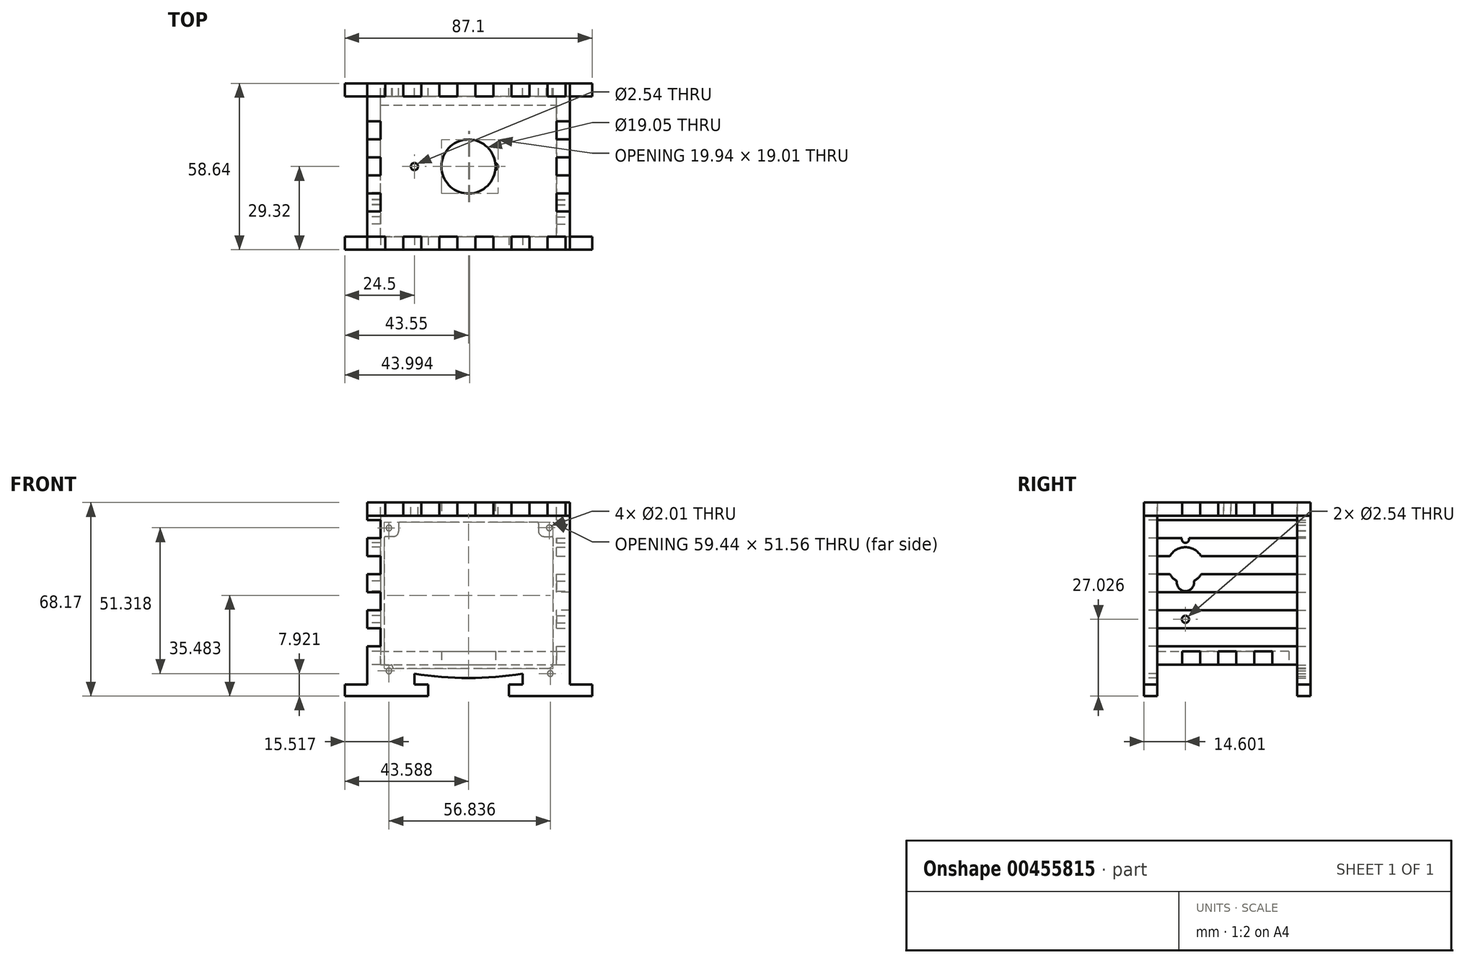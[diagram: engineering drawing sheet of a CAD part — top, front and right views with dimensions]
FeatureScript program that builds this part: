
annotation { "Feature Type Name" : "Feature", "Feature Type Description" : "" }
export const myFeature = defineFeature(function(context is Context, id is Id, definition is map)
    precondition{}
    {
        {
            var Q0;
            Q0=qCreatedBy(makeId("Top.planeOp"),FACE);
            var sketch = newSketch(context, id + "F0", { "sketchPlane" : qUnion([Q0])});
            skLineSegment(sketch, "E0.bottom", {"start": v(-35.67, 29.32) * mm, "end": v(35.67, 29.32) * mm});
            skLineSegment(sketch, "E0.top", {"start": v(-35.67, -29.32) * mm, "end": v(35.67, -29.32) * mm});
            skLineSegment(sketch, "E0.left", {"start": v(-35.67, 29.32) * mm, "end": v(-35.67, -29.32) * mm});
            skLineSegment(sketch, "E0.right", {"start": v(35.67, 29.32) * mm, "end": v(35.67, -29.32) * mm});
            skLineSegment(sketch, "E1", {"start": v(-35.67, 29.32) * mm, "end": v(35.67, -29.32) * mm, "construction": true});
            skSolve(sketch);
        }
        {
            var Q0;
            Q0 = qSketchRegion(id + "F0", true);
            extrude(context, id + "F1", {"entities" : qUnion([Q0]), "offsetDistance" : 25.4 * mm, "depth" : 4.67 * mm});
        }
        {
            var Q0;
            Q0=makeQuery(id+"F1.opExtrude","CAP_FACE",FACE,{"disambiguationData":[OSD([sQuery(id+"F0.wireOp",EDGE,"E0.bottom"),sQuery(id+"F0.wireOp",EDGE,"E0.top"),sQuery(id+"F0.wireOp",EDGE,"E0.left"),sQuery(id+"F0.wireOp",EDGE,"E0.right")])],"isStart":false});
            var sketch = newSketch(context, id + "F2", { "sketchPlane" : qUnion([Q0])});
            skCircle(sketch, "E2", {"center": v(0, 0) * mm, "radius": 2.8 * mm});
            skCircle(sketch, "E3", {"center": v(-19.05, 0) * mm, "radius": 1.27 * mm});
            skCircle(sketch, "E4", {"center": v(9.14, 0) * mm, "radius": 1.27 * mm});
            skSolve(sketch);
        }
        {
            var Q0;
            Q0 = qSketchRegion(id + "F2", true);
            extrude(context, id + "F3", {"entities" : qUnion([Q0]), "operationType" : NewBodyOperationType.REMOVE, "endBound" : BoundingType.THROUGH_ALL, "oppositeDirection" : true, "depth" : 25.4 * mm});
        }
        {
            var Q0;
            Q0=makeQuery(id+"F1.opExtrude","CAP_FACE",FACE,{"disambiguationData":[OSD([sQuery(id+"F0.wireOp",EDGE,"E0.bottom"),sQuery(id+"F0.wireOp",EDGE,"E0.top"),sQuery(id+"F0.wireOp",EDGE,"E0.left"),sQuery(id+"F0.wireOp",EDGE,"E0.right")])],"isStart":false});
            var sketch = newSketch(context, id + "F4", { "sketchPlane" : qUnion([Q0])});
            skArc(sketch, "E5", {"start": v(-5.6, -3) * mm, "mid": v(6.35, 0) * mm, "end": v(-5.6, 3) * mm});
            skArc(sketch, "E6", {"start": v(-5.6, 3) * mm, "mid": v(-9.14, 0) * mm, "end": v(-5.6, -3) * mm});
            skSolve(sketch);
        }
        {
            var Q0;
            Q0 = qSketchRegion(id + "F4", true);
            extrude(context, id + "F5", {"entities" : qUnion([Q0]), "operationType" : NewBodyOperationType.REMOVE, "endBound" : BoundingType.THROUGH_ALL, "oppositeDirection" : true, "depth" : 25.4 * mm});
        }
        {
            var Q0;
            Q0=makeQuery(id+"F1.opExtrude","CAP_FACE",FACE,{"disambiguationData":[OSD([sQuery(id+"F0.wireOp",EDGE,"E0.bottom"),sQuery(id+"F0.wireOp",EDGE,"E0.top"),sQuery(id+"F0.wireOp",EDGE,"E0.left"),sQuery(id+"F0.wireOp",EDGE,"E0.right")])],"isStart":false});
            var sketch = newSketch(context, id + "F6", { "sketchPlane" : qUnion([Q0])});
            skLineSegment(sketch, "E7.bottom", {"start": v(-35.67, 29.32) * mm, "end": v(-29.32, 29.32) * mm});
            skLineSegment(sketch, "E7.top", {"start": v(-35.67, 24.65) * mm, "end": v(-29.32, 24.65) * mm});
            skLineSegment(sketch, "E7.left", {"start": v(-35.67, 29.32) * mm, "end": v(-35.67, 24.65) * mm});
            skLineSegment(sketch, "E7.right", {"start": v(-29.32, 29.32) * mm, "end": v(-29.32, 24.65) * mm});
            skLineSegment(sketch, "E8.1.0.0", {"start": v(-22.97, 29.32) * mm, "end": v(-16.62, 29.32) * mm});
            skLineSegment(sketch, "E8.1.0.1", {"start": v(-22.97, 29.32) * mm, "end": v(-22.97, 24.65) * mm});
            skLineSegment(sketch, "E8.1.0.2", {"start": v(-16.62, 29.32) * mm, "end": v(-16.62, 24.65) * mm});
            skLineSegment(sketch, "E8.1.0.3", {"start": v(-22.97, 24.65) * mm, "end": v(-16.62, 24.65) * mm});
            skLineSegment(sketch, "E8.2.0.0", {"start": v(-10.27, 29.32) * mm, "end": v(-3.92, 29.32) * mm});
            skLineSegment(sketch, "E8.2.0.1", {"start": v(-10.27, 29.32) * mm, "end": v(-10.27, 24.65) * mm});
            skLineSegment(sketch, "E8.2.0.2", {"start": v(-3.92, 29.32) * mm, "end": v(-3.92, 24.65) * mm});
            skLineSegment(sketch, "E8.2.0.3", {"start": v(-10.27, 24.65) * mm, "end": v(-3.92, 24.65) * mm});
            skLineSegment(sketch, "E8.3.0.0", {"start": v(2.43, 29.32) * mm, "end": v(8.78, 29.32) * mm});
            skLineSegment(sketch, "E8.3.0.1", {"start": v(2.43, 29.32) * mm, "end": v(2.43, 24.65) * mm});
            skLineSegment(sketch, "E8.3.0.2", {"start": v(8.78, 29.32) * mm, "end": v(8.78, 24.65) * mm});
            skLineSegment(sketch, "E8.3.0.3", {"start": v(2.43, 24.65) * mm, "end": v(8.78, 24.65) * mm});
            skLineSegment(sketch, "E8.direction1", {"start": v(-35.67, 29.32) * mm, "end": v(-22.97, 29.32) * mm, "construction": true});
            skLineSegment(sketch, "E9.0.4.0", {"start": v(15.13, 29.32) * mm, "end": v(21.48, 29.32) * mm});
            skLineSegment(sketch, "E9.3.4.0", {"start": v(15.13, 29.32) * mm, "end": v(15.13, 24.65) * mm});
            skLineSegment(sketch, "E9.6.4.0", {"start": v(21.48, 29.32) * mm, "end": v(21.48, 24.65) * mm});
            skLineSegment(sketch, "E9.9.4.0", {"start": v(15.13, 24.65) * mm, "end": v(21.48, 24.65) * mm});
            skLineSegment(sketch, "E10.0.5.0", {"start": v(27.83, 29.32) * mm, "end": v(34.18, 29.32) * mm});
            skLineSegment(sketch, "E10.3.5.0", {"start": v(27.83, 29.32) * mm, "end": v(27.83, 24.65) * mm});
            skLineSegment(sketch, "E10.6.5.0", {"start": v(34.18, 29.32) * mm, "end": v(34.18, 24.65) * mm});
            skLineSegment(sketch, "E10.9.5.0", {"start": v(27.83, 24.65) * mm, "end": v(34.18, 24.65) * mm});
            skSolve(sketch);
        }
        {
            var Q0;
            Q0 = qSketchRegion(id + "F6", true);
            extrude(context, id + "F7", {"entities" : qUnion([Q0]), "operationType" : NewBodyOperationType.REMOVE, "oppositeDirection" : true, "depth" : 25.4 * mm});
        }
        {
            var Q0;
            Q0=makeQuery(id+"F1.opExtrude","CAP_FACE",FACE,{"disambiguationData":[OSD([sQuery(id+"F0.wireOp",EDGE,"E0.bottom"),sQuery(id+"F0.wireOp",EDGE,"E0.top"),sQuery(id+"F0.wireOp",EDGE,"E0.left"),sQuery(id+"F0.wireOp",EDGE,"E0.right")])],"isStart":false});
            var sketch = newSketch(context, id + "F8", { "sketchPlane" : qUnion([Q0])});
            skLineSegment(sketch, "E11.0.1.0", {"start": v(-35.67, -15.88) * mm, "end": v(-31, -15.88) * mm});
            skLineSegment(sketch, "E11.0.1.1", {"start": v(-31, -15.88) * mm, "end": v(-31, -9.53) * mm});
            skLineSegment(sketch, "E11.0.1.2", {"start": v(-35.67, -15.88) * mm, "end": v(-35.67, -9.53) * mm});
            skLineSegment(sketch, "E11.0.1.3", {"start": v(-35.67, -9.53) * mm, "end": v(-31, -9.53) * mm});
            skLineSegment(sketch, "E11.0.2.0", {"start": v(-35.67, -3.18) * mm, "end": v(-31, -3.18) * mm});
            skLineSegment(sketch, "E11.0.2.1", {"start": v(-31, -3.18) * mm, "end": v(-31, 3.17) * mm});
            skLineSegment(sketch, "E11.0.2.2", {"start": v(-35.67, -3.18) * mm, "end": v(-35.67, 3.17) * mm});
            skLineSegment(sketch, "E11.0.2.3", {"start": v(-35.67, 3.17) * mm, "end": v(-31, 3.17) * mm});
            skLineSegment(sketch, "E11.0.3.0", {"start": v(-35.67, 9.52) * mm, "end": v(-31, 9.52) * mm});
            skLineSegment(sketch, "E11.0.3.1", {"start": v(-31, 9.52) * mm, "end": v(-31, 15.87) * mm});
            skLineSegment(sketch, "E11.0.3.2", {"start": v(-35.67, 9.52) * mm, "end": v(-35.67, 15.87) * mm});
            skLineSegment(sketch, "E11.0.3.3", {"start": v(-35.67, 15.87) * mm, "end": v(-31, 15.87) * mm});
            skSolve(sketch);
        }
        {
            var Q0;
            Q0 = qSketchRegion(id + "F8", true);
            extrude(context, id + "F9", {"entities" : qUnion([Q0]), "operationType" : NewBodyOperationType.REMOVE, "endBound" : BoundingType.THROUGH_ALL, "oppositeDirection" : true, "depth" : 25.4 * mm});
        }
        {
            var Q0;
            Q0=makeQuery(id+"F9.boolean.opBoolean","COPY",FACE,{"derivedFrom":makeQuery(id+"F9.opExtrude","SWEPT_FACE",FACE,{"disambiguationData":[OSD([sQuery(id+"F8.wireOp",EDGE,"E11.0.3.1")])]})});
            var sketch = newSketch(context, id + "F10", { "sketchPlane" : qUnion([Q0])});
            skLineSegment(sketch, "E12.bottom", {"start": v(29.32, 4.67) * mm, "end": v(-29.32, 4.67) * mm});
            skLineSegment(sketch, "E12.top", {"start": v(29.32, -52.45) * mm, "end": v(-29.32, -52.45) * mm});
            skLineSegment(sketch, "E12.left", {"start": v(29.32, 4.67) * mm, "end": v(29.32, -52.45) * mm});
            skLineSegment(sketch, "E12.right", {"start": v(-29.32, 4.67) * mm, "end": v(-29.32, -52.45) * mm});
            skSolve(sketch);
        }
        {
            var Q0;
            Q0 = qSketchRegion(id + "F10", true);
            var Q1;
            {var subQ1=sQuery(id+"F0.wireOp",EDGE,"E0.left");Q1=makeQuery(id+"F9.boolean.opBoolean","SPLIT",FACE,{"disambiguationData":[TD([makeQuery(id+"F9.opExtrude","SWEPT_FACE",FACE,{"disambiguationData":[OSD([sQuery(id+"F8.wireOp",EDGE,"E11.0.2.3")])]})])],"derivedFrom":makeQuery(id+"F1.opExtrude","SWEPT_FACE",FACE,{"disambiguationData":[OSD([subQ1])]})});}
            extrude(context, id + "F11", {"entities" : qUnion([Q0]), "endBound" : BoundingType.UP_TO_SURFACE, "endBoundEntityFace" : qUnion([Q1]), "depth" : 25.4 * mm});
        }
        {
            var Q0;
            Q0=makeQuery(id+"F1.opExtrude","SWEPT_BODY",BODY,{"disambiguationData":[OSD([sQuery(id+"F0.wireOp",EDGE,"E0.bottom"),sQuery(id+"F0.wireOp",EDGE,"E0.top"),sQuery(id+"F0.wireOp",EDGE,"E0.left"),sQuery(id+"F0.wireOp",EDGE,"E0.right")])]});
            var Q1;
            Q1=makeQuery(id+"F11.opExtrude","SWEPT_BODY",BODY,{"disambiguationData":[OSD([sQuery(id+"F10.wireOp",EDGE,"E12.bottom"),sQuery(id+"F10.wireOp",EDGE,"E12.top"),sQuery(id+"F10.wireOp",EDGE,"E12.left"),sQuery(id+"F10.wireOp",EDGE,"E12.right")])]});
            booleanBodies(context, id + "F12", {"operationType" : BooleanOperationType.SUBTRACTION, "tools" : qUnion([Q0]), "targets" : qUnion([Q1]), "keepTools" : true});
        }
        {
            var Q0;
            Q0=makeQuery(id+"F11.opExtrude","CAP_FACE",FACE,{"disambiguationData":[OSD([sQuery(id+"F10.wireOp",EDGE,"E12.bottom"),sQuery(id+"F10.wireOp",EDGE,"E12.top"),sQuery(id+"F10.wireOp",EDGE,"E12.left"),sQuery(id+"F10.wireOp",EDGE,"E12.right")])],"isStart":false});
            var sketch = newSketch(context, id + "F13", { "sketchPlane" : qUnion([Q0])});
            skCircle(sketch, "E13", {"center": v(14.72, -8.28) * mm, "radius": 1.27 * mm});
            skCircle(sketch, "E14", {"center": v(14.72, -17.42) * mm, "radius": 2.8 * mm});
            skCircle(sketch, "E15", {"center": v(14.72, -36.47) * mm, "radius": 1.27 * mm});
            skSolve(sketch);
        }
        {
            var Q0;
            Q0 = qSketchRegion(id + "F13", true);
            extrude(context, id + "F14", {"entities" : qUnion([Q0]), "operationType" : NewBodyOperationType.REMOVE, "endBound" : BoundingType.THROUGH_ALL, "oppositeDirection" : true, "depth" : 25.4 * mm});
        }
        {
            var Q0;
            Q0=makeQuery(id+"F11.opExtrude","CAP_FACE",FACE,{"disambiguationData":[OSD([sQuery(id+"F10.wireOp",EDGE,"E12.bottom"),sQuery(id+"F10.wireOp",EDGE,"E12.top"),sQuery(id+"F10.wireOp",EDGE,"E12.left"),sQuery(id+"F10.wireOp",EDGE,"E12.right")])],"isStart":false});
            var sketch = newSketch(context, id + "F15", { "sketchPlane" : qUnion([Q0])});
            skArc(sketch, "E16", {"start": v(17.73, -23.02) * mm, "mid": v(14.72, -11.07) * mm, "end": v(11.71, -23.02) * mm});
            skArc(sketch, "E17", {"start": v(11.71, -23.02) * mm, "mid": v(14.72, -26.57) * mm, "end": v(17.73, -23.02) * mm});
            skSolve(sketch);
        }
        {
            var Q0;
            Q0 = qSketchRegion(id + "F15", true);
            extrude(context, id + "F16", {"entities" : qUnion([Q0]), "operationType" : NewBodyOperationType.REMOVE, "endBound" : BoundingType.THROUGH_ALL, "oppositeDirection" : true, "depth" : 25.4 * mm});
        }
        {
            var Q0;
            {var subQ3=sQuery(id+"F0.wireOp",EDGE,"E0.bottom");Q0=makeQuery(id+"F7.boolean.opBoolean","SPLIT",FACE,{"disambiguationData":[TD([makeQuery(id+"F7.opExtrude","SWEPT_FACE",FACE,{"disambiguationData":[OSD([sQuery(id+"F6.wireOp",EDGE,"E8.2.0.2")])]})])],"derivedFrom":makeQuery(id+"F1.opExtrude","SWEPT_FACE",FACE,{"disambiguationData":[OSD([subQ3])]})});}
            var sketch = newSketch(context, id + "F17", { "sketchPlane" : qUnion([Q0])});
            skLineSegment(sketch, "E18.bottom", {"start": v(35.67, 4.67) * mm, "end": v(-35.67, 4.67) * mm});
            skLineSegment(sketch, "E18.top", {"start": v(35.67, -63.5) * mm, "end": v(-35.67, -63.5) * mm});
            skLineSegment(sketch, "E18.left", {"start": v(35.67, 4.67) * mm, "end": v(35.67, -63.5) * mm});
            skLineSegment(sketch, "E18.right", {"start": v(-35.67, 4.67) * mm, "end": v(-35.67, -63.5) * mm});
            skSolve(sketch);
        }
        {
            var Q0;
            Q0 = qSketchRegion(id + "F17", true);
            var Q1;
            Q1=makeQuery(id+"F7.boolean.opBoolean","COPY",FACE,{"derivedFrom":makeQuery(id+"F7.opExtrude","SWEPT_FACE",FACE,{"disambiguationData":[OSD([sQuery(id+"F6.wireOp",EDGE,"E8.3.0.3")])]})});
            extrude(context, id + "F18", {"entities" : qUnion([Q0]), "endBound" : BoundingType.UP_TO_SURFACE, "oppositeDirection" : true, "endBoundEntityFace" : qUnion([Q1]), "depth" : 25.4 * mm, "offsetDistance" : 25.4 * mm});
        }
        {
            var Q0;
            Q0=makeQuery(id+"F18.opExtrude","CAP_FACE",FACE,{"disambiguationData":[OSD([sQuery(id+"F17.wireOp",EDGE,"E18.bottom"),sQuery(id+"F17.wireOp",EDGE,"E18.top"),sQuery(id+"F17.wireOp",EDGE,"E18.left"),sQuery(id+"F17.wireOp",EDGE,"E18.right")])],"isStart":true});
            var sketch = newSketch(context, id + "F19", { "sketchPlane" : qUnion([Q0])});
            skLineSegment(sketch, "E19", {"start": v(-14.22, -63.5) * mm, "end": v(-14.22, -59.48) * mm});
            skLineSegment(sketch, "E20", {"start": v(-14.22, -59.48) * mm, "end": v(-19.05, -59.48) * mm});
            skLineSegment(sketch, "E21", {"start": v(-19.05, -59.48) * mm, "end": v(-19.05, -55.63) * mm});
            skLineSegment(sketch, "E22", {"start": v(19.05, -55.63) * mm, "end": v(19.05, -59.44) * mm});
            skLineSegment(sketch, "E23", {"start": v(19.05, -59.44) * mm, "end": v(14.22, -59.44) * mm});
            skLineSegment(sketch, "E24", {"start": v(14.22, -59.44) * mm, "end": v(14.22, -63.5) * mm});
            skLineSegment(sketch, "E25", {"start": v(14.22, -63.5) * mm, "end": v(-14.22, -63.5) * mm});
            skArc(sketch, "E26", {"start": v(-19.05, -55.63) * mm, "mid": v(0, -57.17) * mm, "end": v(19.05, -55.63) * mm});
            skArc(sketch, "E27", {"start": v(-19.05, -55.63) * mm, "mid": v(0, -57.22) * mm, "end": v(19.05, -55.63) * mm});
            skSolve(sketch);
        }
        {
            var Q0;
            Q0 = qSketchRegion(id + "F19", true);
            extrude(context, id + "F20", {"entities" : qUnion([Q0]), "operationType" : NewBodyOperationType.REMOVE, "endBound" : BoundingType.THROUGH_ALL, "oppositeDirection" : true, "depth" : 25.4 * mm});
        }
        {
            var Q0;
            Q0=makeQuery(id+"F18.opExtrude","CAP_FACE",FACE,{"disambiguationData":[OSD([sQuery(id+"F17.wireOp",EDGE,"E18.bottom"),sQuery(id+"F17.wireOp",EDGE,"E18.top"),sQuery(id+"F17.wireOp",EDGE,"E18.left"),sQuery(id+"F17.wireOp",EDGE,"E18.right")])],"isStart":true});
            var sketch = newSketch(context, id + "F21", { "sketchPlane" : qUnion([Q0])});
            skLineSegment(sketch, "E28.bottom", {"start": v(35.67, -63.5) * mm, "end": v(43.55, -63.5) * mm});
            skLineSegment(sketch, "E28.top", {"start": v(35.67, -59.44) * mm, "end": v(43.55, -59.44) * mm});
            skLineSegment(sketch, "E28.left", {"start": v(35.67, -63.5) * mm, "end": v(35.67, -59.44) * mm});
            skLineSegment(sketch, "E28.right", {"start": v(43.55, -63.5) * mm, "end": v(43.55, -59.44) * mm});
            skLineSegment(sketch, "E29.bottom", {"start": v(-35.67, -63.5) * mm, "end": v(-43.55, -63.5) * mm});
            skLineSegment(sketch, "E29.top", {"start": v(-35.67, -59.44) * mm, "end": v(-43.55, -59.44) * mm});
            skLineSegment(sketch, "E29.left", {"start": v(-35.67, -63.5) * mm, "end": v(-35.67, -59.44) * mm});
            skLineSegment(sketch, "E29.right", {"start": v(-43.55, -63.5) * mm, "end": v(-43.55, -59.44) * mm});
            skSolve(sketch);
        }
        {
            var Q0;
            Q0 = qSketchRegion(id + "F21", true);
            var Q1;
            Q1=makeQuery(id+"F18.opExtrude","CAP_FACE",FACE,{"disambiguationData":[OSD([sQuery(id+"F17.wireOp",EDGE,"E18.bottom"),sQuery(id+"F17.wireOp",EDGE,"E18.top"),sQuery(id+"F17.wireOp",EDGE,"E18.left"),sQuery(id+"F17.wireOp",EDGE,"E18.right")])],"isStart":false});
            extrude(context, id + "F22", {"entities" : qUnion([Q0]), "operationType" : NewBodyOperationType.ADD, "endBound" : BoundingType.UP_TO_SURFACE, "oppositeDirection" : true, "endBoundEntityFace" : qUnion([Q1]), "depth" : 25.4 * mm, "offsetDistance" : 25.4 * mm});
        }
        {
            var Q0;
            Q0=makeQuery(id+"F1.opExtrude","SWEPT_BODY",BODY,{"disambiguationData":[OSD([sQuery(id+"F0.wireOp",EDGE,"E0.bottom"),sQuery(id+"F0.wireOp",EDGE,"E0.top"),sQuery(id+"F0.wireOp",EDGE,"E0.left"),sQuery(id+"F0.wireOp",EDGE,"E0.right")])]});
            var Q1;
            Q1=makeQuery(id+"F18.opExtrude","SWEPT_BODY",BODY,{"disambiguationData":[OSD([sQuery(id+"F17.wireOp",EDGE,"E18.bottom"),sQuery(id+"F17.wireOp",EDGE,"E18.top"),sQuery(id+"F17.wireOp",EDGE,"E18.left"),sQuery(id+"F17.wireOp",EDGE,"E18.right")])]});
            booleanBodies(context, id + "F23", {"operationType" : BooleanOperationType.SUBTRACTION, "tools" : qUnion([Q0]), "targets" : qUnion([Q1]), "keepTools" : true});
        }
        {
            var Q0;
            Q0=makeQuery(id+"F22.boolean.opBoolean","MERGE",FACE,{"derivedFrom":[makeQuery(id+"F18.opExtrude","CAP_FACE",FACE,{"disambiguationData":[OSD([sQuery(id+"F17.wireOp",EDGE,"E18.bottom"),sQuery(id+"F17.wireOp",EDGE,"E18.top"),sQuery(id+"F17.wireOp",EDGE,"E18.left"),sQuery(id+"F17.wireOp",EDGE,"E18.right")])],"isStart":true}),makeQuery(id+"F22.opExtrude","CAP_FACE",FACE,{"disambiguationData":[OSD([sQuery(id+"F21.wireOp",EDGE,"E28.bottom"),sQuery(id+"F21.wireOp",EDGE,"E28.top"),sQuery(id+"F21.wireOp",EDGE,"E28.left"),sQuery(id+"F21.wireOp",EDGE,"E28.right")])],"isStart":true}),makeQuery(id+"F22.opExtrude","CAP_FACE",FACE,{"disambiguationData":[OSD([sQuery(id+"F21.wireOp",EDGE,"E29.bottom"),sQuery(id+"F21.wireOp",EDGE,"E29.top"),sQuery(id+"F21.wireOp",EDGE,"E29.left"),sQuery(id+"F21.wireOp",EDGE,"E29.right")])],"isStart":true})]});
            var sketch = newSketch(context, id + "F24", { "sketchPlane" : qUnion([Q0])});
            skLineSegment(sketch, "E30", {"start": v(35.67, -27.38) * mm, "end": v(22.88, -27.38) * mm, "construction": true});
            skPoint(sketch, "E30.endSnap0", {"position": v(35.67, -27.38) * mm});
            skLineSegment(sketch, "E31.bottom", {"start": v(35.67, -26.92) * mm, "end": v(31, -26.92) * mm});
            skLineSegment(sketch, "E31.top", {"start": v(35.67, -33.27) * mm, "end": v(31, -33.27) * mm});
            skLineSegment(sketch, "E31.left", {"start": v(35.67, -26.92) * mm, "end": v(35.67, -33.27) * mm});
            skLineSegment(sketch, "E31.right", {"start": v(31, -26.92) * mm, "end": v(31, -33.27) * mm});
            skLineSegment(sketch, "E32.bottom", {"start": v(31, -20.57) * mm, "end": v(35.67, -20.57) * mm});
            skLineSegment(sketch, "E32.top", {"start": v(31, -14.22) * mm, "end": v(35.67, -14.22) * mm});
            skLineSegment(sketch, "E32.left", {"start": v(31, -20.57) * mm, "end": v(31, -14.22) * mm});
            skLineSegment(sketch, "E32.right", {"start": v(35.67, -20.57) * mm, "end": v(35.67, -14.22) * mm});
            skLineSegment(sketch, "E33.0.1.0", {"start": v(31, -1.52) * mm, "end": v(35.67, -1.52) * mm});
            skLineSegment(sketch, "E33.0.1.1", {"start": v(31, -7.87) * mm, "end": v(31, -1.52) * mm});
            skLineSegment(sketch, "E33.0.1.2", {"start": v(35.67, -7.87) * mm, "end": v(35.67, -1.52) * mm});
            skLineSegment(sketch, "E33.0.1.3", {"start": v(31, -7.87) * mm, "end": v(35.67, -7.87) * mm});
            skLineSegment(sketch, "E33.direction1", {"start": v(31, -14.22) * mm, "end": v(53.97, -14.22) * mm, "construction": true});
            skLineSegment(sketch, "E33.direction2", {"start": v(31, -14.22) * mm, "end": v(31, -1.52) * mm, "construction": true});
            skLineSegment(sketch, "E34.MirrorCS", {"start": v(31, -40.54) * mm, "end": v(31, -53.24) * mm, "construction": true});
            skLineSegment(sketch, "E35.bottom", {"start": v(31, -39.62) * mm, "end": v(35.67, -39.62) * mm});
            skLineSegment(sketch, "E35.top", {"start": v(31, -45.97) * mm, "end": v(35.67, -45.97) * mm});
            skLineSegment(sketch, "E35.left", {"start": v(31, -39.62) * mm, "end": v(31, -45.97) * mm});
            skLineSegment(sketch, "E35.right", {"start": v(35.67, -39.62) * mm, "end": v(35.67, -45.97) * mm});
            skSolve(sketch);
        }
        {
            var Q0;
            Q0 = qSketchRegion(id + "F24", true);
            extrude(context, id + "F25", {"entities" : qUnion([Q0]), "operationType" : NewBodyOperationType.REMOVE, "endBound" : BoundingType.THROUGH_ALL, "oppositeDirection" : true, "depth" : 25.4 * mm});
        }
        {
            var Q0;
            Q0=makeQuery(id+"F18.opExtrude","SWEPT_BODY",BODY,{"disambiguationData":[OSD([sQuery(id+"F17.wireOp",EDGE,"E18.bottom"),sQuery(id+"F17.wireOp",EDGE,"E18.top"),sQuery(id+"F17.wireOp",EDGE,"E18.left"),sQuery(id+"F17.wireOp",EDGE,"E18.right")])]});
            var Q1;
            Q1=makeQuery(id+"F11.opExtrude","SWEPT_BODY",BODY,{"disambiguationData":[OSD([sQuery(id+"F10.wireOp",EDGE,"E12.bottom"),sQuery(id+"F10.wireOp",EDGE,"E12.top"),sQuery(id+"F10.wireOp",EDGE,"E12.left"),sQuery(id+"F10.wireOp",EDGE,"E12.right")])]});
            booleanBodies(context, id + "F26", {"operationType" : BooleanOperationType.SUBTRACTION, "tools" : qUnion([Q0]), "targets" : qUnion([Q1]), "keepTools" : true});
        }
        {
            var Q0;
            Q0=makeQuery(id+"F11.opExtrude","CAP_FACE",FACE,{"disambiguationData":[OSD([sQuery(id+"F10.wireOp",EDGE,"E12.bottom"),sQuery(id+"F10.wireOp",EDGE,"E12.top"),sQuery(id+"F10.wireOp",EDGE,"E12.left"),sQuery(id+"F10.wireOp",EDGE,"E12.right")])],"isStart":false});
            var sketch = newSketch(context, id + "F27", { "sketchPlane" : qUnion([Q0])});
            skLineSegment(sketch, "E36.bottom", {"start": v(-15.87, -47.78) * mm, "end": v(-9.52, -47.78) * mm});
            skLineSegment(sketch, "E36.top", {"start": v(-15.87, -52.45) * mm, "end": v(-9.52, -52.45) * mm});
            skLineSegment(sketch, "E36.left", {"start": v(-15.87, -47.78) * mm, "end": v(-15.87, -52.45) * mm});
            skLineSegment(sketch, "E36.right", {"start": v(-9.52, -47.78) * mm, "end": v(-9.52, -52.45) * mm});
            skLineSegment(sketch, "E37.bottom", {"start": v(-3.17, -47.78) * mm, "end": v(3.18, -47.78) * mm});
            skLineSegment(sketch, "E37.top", {"start": v(-3.17, -52.45) * mm, "end": v(3.18, -52.45) * mm});
            skLineSegment(sketch, "E37.left", {"start": v(-3.17, -47.78) * mm, "end": v(-3.17, -52.45) * mm});
            skLineSegment(sketch, "E37.right", {"start": v(3.18, -47.78) * mm, "end": v(3.18, -52.45) * mm});
            skLineSegment(sketch, "E38.bottom", {"start": v(9.53, -47.78) * mm, "end": v(15.88, -47.78) * mm});
            skLineSegment(sketch, "E38.top", {"start": v(9.53, -52.45) * mm, "end": v(15.88, -52.45) * mm});
            skLineSegment(sketch, "E38.left", {"start": v(9.53, -47.78) * mm, "end": v(9.53, -52.45) * mm});
            skLineSegment(sketch, "E38.right", {"start": v(15.88, -47.78) * mm, "end": v(15.88, -52.45) * mm});
            skSolve(sketch);
        }
        {
            var Q0;
            Q0 = qSketchRegion(id + "F27", true);
            var Q1;
            Q1=makeQuery(id+"F11.opExtrude","CAP_FACE",FACE,{"disambiguationData":[OSD([sQuery(id+"F10.wireOp",EDGE,"E12.bottom"),sQuery(id+"F10.wireOp",EDGE,"E12.top"),sQuery(id+"F10.wireOp",EDGE,"E12.left"),sQuery(id+"F10.wireOp",EDGE,"E12.right")])],"isStart":true});
            extrude(context, id + "F28", {"entities" : qUnion([Q0]), "operationType" : NewBodyOperationType.REMOVE, "endBound" : BoundingType.UP_TO_SURFACE, "oppositeDirection" : true, "depth" : 25.4 * mm, "endBoundEntityFace" : qUnion([Q1]), "offsetDistance" : 25.4 * mm});
        }
        {
            var Q0;
            Q0=makeQuery(id+"F11.opExtrude","SWEPT_BODY",BODY,{"disambiguationData":[OSD([sQuery(id+"F10.wireOp",EDGE,"E12.bottom"),sQuery(id+"F10.wireOp",EDGE,"E12.top"),sQuery(id+"F10.wireOp",EDGE,"E12.left"),sQuery(id+"F10.wireOp",EDGE,"E12.right")])]});
            var Q1;
            Q1=qCreatedBy(makeId("Right.planeOp"),FACE);
            mirror(context, id + "F29", {"entities" : qUnion([Q0]), "mirrorPlane" : qUnion([Q1])});
        }
        {
            var Q0;
            Q0=makeQuery(id+"F29.opPattern","COPY",BODY,{"derivedFrom":makeQuery(id+"F11.opExtrude","SWEPT_BODY",BODY,{"disambiguationData":[OSD([sQuery(id+"F10.wireOp",EDGE,"E12.bottom"),sQuery(id+"F10.wireOp",EDGE,"E12.top"),sQuery(id+"F10.wireOp",EDGE,"E12.left"),sQuery(id+"F10.wireOp",EDGE,"E12.right")])]}),"instanceName":"1"});
            var Q1;
            Q1=makeQuery(id+"F18.opExtrude","SWEPT_BODY",BODY,{"disambiguationData":[OSD([sQuery(id+"F17.wireOp",EDGE,"E18.bottom"),sQuery(id+"F17.wireOp",EDGE,"E18.top"),sQuery(id+"F17.wireOp",EDGE,"E18.left"),sQuery(id+"F17.wireOp",EDGE,"E18.right")])]});
            booleanBodies(context, id + "F30", {"operationType" : BooleanOperationType.SUBTRACTION, "tools" : qUnion([Q0]), "targets" : qUnion([Q1]), "keepTools" : true});
        }
        {
            var Q0;
            Q0=makeQuery(id+"F18.opExtrude","SWEPT_BODY",BODY,{"disambiguationData":[OSD([sQuery(id+"F17.wireOp",EDGE,"E18.bottom"),sQuery(id+"F17.wireOp",EDGE,"E18.top"),sQuery(id+"F17.wireOp",EDGE,"E18.left"),sQuery(id+"F17.wireOp",EDGE,"E18.right")])]});
            var Q1;
            Q1=qCreatedBy(makeId("Front.planeOp"),FACE);
            mirror(context, id + "F31", {"entities" : qUnion([Q0]), "mirrorPlane" : qUnion([Q1])});
        }
        {
            var Q0;
            Q0=makeQuery(id+"F22.boolean.opBoolean","MERGE",FACE,{"derivedFrom":[makeQuery(id+"F18.opExtrude","CAP_FACE",FACE,{"disambiguationData":[OSD([sQuery(id+"F17.wireOp",EDGE,"E18.bottom"),sQuery(id+"F17.wireOp",EDGE,"E18.top"),sQuery(id+"F17.wireOp",EDGE,"E18.left"),sQuery(id+"F17.wireOp",EDGE,"E18.right")])],"isStart":true}),makeQuery(id+"F22.opExtrude","CAP_FACE",FACE,{"disambiguationData":[OSD([sQuery(id+"F21.wireOp",EDGE,"E28.bottom"),sQuery(id+"F21.wireOp",EDGE,"E28.top"),sQuery(id+"F21.wireOp",EDGE,"E28.left"),sQuery(id+"F21.wireOp",EDGE,"E28.right")])],"isStart":true}),makeQuery(id+"F22.opExtrude","CAP_FACE",FACE,{"disambiguationData":[OSD([sQuery(id+"F21.wireOp",EDGE,"E29.bottom"),sQuery(id+"F21.wireOp",EDGE,"E29.top"),sQuery(id+"F21.wireOp",EDGE,"E29.left"),sQuery(id+"F21.wireOp",EDGE,"E29.right")])],"isStart":true})]});
            var sketch = newSketch(context, id + "F32", { "sketchPlane" : qUnion([Q0])});
            skLineSegment(sketch, "E39", {"start": v(0, 8) * mm, "end": v(0, -66.28) * mm, "construction": true});
            skCircle(sketch, "E40", {"center": v(-27.74, -4.01) * mm, "radius": 1 * mm});
            skPoint(sketch, "E40.centerSnap0", {"position": v(-33.34, -5.9) * mm});
            skCircle(sketch, "E41", {"center": v(27.74, -4.01) * mm, "radius": 1 * mm});
            skCircle(sketch, "E42", {"center": v(28.75, -55.37) * mm, "radius": 1 * mm});
            skCircle(sketch, "E43", {"center": v(-29.2, -55.9) * mm, "radius": 1 * mm});
            skSolve(sketch);
        }
        {
            var Q0;
            Q0=makeQuery(id+"F22.boolean.opBoolean","MERGE",FACE,{"derivedFrom":[makeQuery(id+"F18.opExtrude","CAP_FACE",FACE,{"disambiguationData":[OSD([sQuery(id+"F17.wireOp",EDGE,"E18.bottom"),sQuery(id+"F17.wireOp",EDGE,"E18.top"),sQuery(id+"F17.wireOp",EDGE,"E18.left"),sQuery(id+"F17.wireOp",EDGE,"E18.right")])],"isStart":true}),makeQuery(id+"F22.opExtrude","CAP_FACE",FACE,{"disambiguationData":[OSD([sQuery(id+"F21.wireOp",EDGE,"E28.bottom"),sQuery(id+"F21.wireOp",EDGE,"E28.top"),sQuery(id+"F21.wireOp",EDGE,"E28.left"),sQuery(id+"F21.wireOp",EDGE,"E28.right")])],"isStart":true}),makeQuery(id+"F22.opExtrude","CAP_FACE",FACE,{"disambiguationData":[OSD([sQuery(id+"F21.wireOp",EDGE,"E29.bottom"),sQuery(id+"F21.wireOp",EDGE,"E29.top"),sQuery(id+"F21.wireOp",EDGE,"E29.left"),sQuery(id+"F21.wireOp",EDGE,"E29.right")])],"isStart":true})]});
            var sketch = newSketch(context, id + "F33", { "sketchPlane" : qUnion([Q0])});
            skLineSegment(sketch, "E44.bottom", {"start": v(-24.17, -2.24) * mm, "end": v(24.1, -2.24) * mm});
            skLineSegment(sketch, "E44.top", {"start": v(-27.85, -53.8) * mm, "end": v(26.24, -53.8) * mm});
            skLineSegment(sketch, "E44.left", {"start": v(-29.76, -7.82) * mm, "end": v(-29.76, -51.9) * mm});
            skLineSegment(sketch, "E44.right", {"start": v(29.68, -7.82) * mm, "end": v(29.68, -52.02) * mm});
            skPoint(sketch, "E45", {"position": v(-27.72, -4.27) * mm});
            skLineSegment(sketch, "E46", {"start": v(-24.68, -2.74) * mm, "end": v(-24.68, -5.41) * mm});
            skLineSegment(sketch, "E47", {"start": v(-26.58, -7.32) * mm, "end": v(-29.25, -7.32) * mm});
            skLineSegment(sketch, "E48", {"start": v(24.6, -2.74) * mm, "end": v(24.6, -5.41) * mm});
            skLineSegment(sketch, "E49", {"start": v(26.5, -7.32) * mm, "end": v(29.17, -7.32) * mm});
            skPoint(sketch, "E50.visualSharp", {"position": v(-24.68, -7.32) * mm});
            skArc(sketch, "E50.filletArc", {"start": v(-26.58, -7.32) * mm, "mid": v(-25.23, -6.76) * mm, "end": v(-24.68, -5.41) * mm});
            skPoint(sketch, "E51.visualSharp", {"position": v(24.6, -7.32) * mm});
            skArc(sketch, "E51.filletArc", {"start": v(24.6, -5.41) * mm, "mid": v(25.16, -6.76) * mm, "end": v(26.5, -7.32) * mm});
            skPoint(sketch, "E52.visualSharp", {"position": v(-29.76, -53.8) * mm});
            skArc(sketch, "E52.filletArc", {"start": v(-29.76, -51.9) * mm, "mid": v(-29.2, -53.24) * mm, "end": v(-27.85, -53.8) * mm});
            skPoint(sketch, "E53.visualSharp", {"position": v(29.68, -53.8) * mm});
            skCircle(sketch, "E54", {"center": v(28.03, -4.32) * mm, "radius": 1 * mm});
            skCircle(sketch, "E55", {"center": v(-28.45, -4.26) * mm, "radius": 1 * mm});
            skCircle(sketch, "E56", {"center": v(-28.8, -55.58) * mm, "radius": 1 * mm});
            skCircle(sketch, "E57", {"center": v(28.02, -54.66) * mm, "radius": 1 * mm});
            skLineSegment(sketch, "E58", {"start": v(29.17, -52.53) * mm, "end": v(27.26, -52.53) * mm});
            skLineSegment(sketch, "E59", {"start": v(26.75, -53.04) * mm, "end": v(26.75, -53.29) * mm});
            skArc(sketch, "E60.filletArc", {"start": v(29.17, -52.53) * mm, "mid": v(29.53, -52.38) * mm, "end": v(29.68, -52.02) * mm});
            skPoint(sketch, "E61.visualSharp", {"position": v(26.75, -52.53) * mm});
            skArc(sketch, "E61.filletArc", {"start": v(27.26, -52.53) * mm, "mid": v(26.9, -52.68) * mm, "end": v(26.75, -53.04) * mm});
            skArc(sketch, "E62.filletArc", {"start": v(26.24, -53.8) * mm, "mid": v(26.6, -53.65) * mm, "end": v(26.75, -53.29) * mm});
            skPoint(sketch, "E63.visualSharp", {"position": v(-24.68, -2.24) * mm});
            skArc(sketch, "E63.filletArc", {"start": v(-24.17, -2.24) * mm, "mid": v(-24.53, -2.38) * mm, "end": v(-24.68, -2.74) * mm});
            skPoint(sketch, "E64.visualSharp", {"position": v(-29.76, -7.32) * mm});
            skArc(sketch, "E64.filletArc", {"start": v(-29.25, -7.32) * mm, "mid": v(-29.6, -7.46) * mm, "end": v(-29.76, -7.82) * mm});
            skPoint(sketch, "E65.visualSharp", {"position": v(24.6, -2.24) * mm});
            skArc(sketch, "E65.filletArc", {"start": v(24.6, -2.74) * mm, "mid": v(24.45, -2.38) * mm, "end": v(24.1, -2.24) * mm});
            skPoint(sketch, "E66.visualSharp", {"position": v(29.68, -7.32) * mm});
            skArc(sketch, "E66.filletArc", {"start": v(29.68, -7.82) * mm, "mid": v(29.53, -7.46) * mm, "end": v(29.17, -7.32) * mm});
            skSolve(sketch);
        }
        {
            var Q0;
            Q0 = qSketchRegion(id + "F33", true);
            var Q1;
            Q1=makeQuery(id+"F22.boolean.opBoolean","MERGE",FACE,{"derivedFrom":[makeQuery(id+"F18.opExtrude","CAP_FACE",FACE,{"disambiguationData":[OSD([sQuery(id+"F17.wireOp",EDGE,"E18.bottom"),sQuery(id+"F17.wireOp",EDGE,"E18.top"),sQuery(id+"F17.wireOp",EDGE,"E18.left"),sQuery(id+"F17.wireOp",EDGE,"E18.right")])],"isStart":false}),makeQuery(id+"F22.opExtrude","CAP_FACE",FACE,{"disambiguationData":[OSD([sQuery(id+"F21.wireOp",EDGE,"E28.bottom"),sQuery(id+"F21.wireOp",EDGE,"E28.top"),sQuery(id+"F21.wireOp",EDGE,"E28.left"),sQuery(id+"F21.wireOp",EDGE,"E28.right")])],"isStart":false}),makeQuery(id+"F22.opExtrude","CAP_FACE",FACE,{"disambiguationData":[OSD([sQuery(id+"F21.wireOp",EDGE,"E29.bottom"),sQuery(id+"F21.wireOp",EDGE,"E29.top"),sQuery(id+"F21.wireOp",EDGE,"E29.left"),sQuery(id+"F21.wireOp",EDGE,"E29.right")])],"isStart":false})]});
            extrude(context, id + "F34", {"entities" : qUnion([Q0]), "operationType" : NewBodyOperationType.REMOVE, "endBound" : BoundingType.UP_TO_SURFACE, "oppositeDirection" : true, "endBoundEntityFace" : qUnion([Q1]), "depth" : 25.4 * mm, "offsetDistance" : 25.4 * mm});
        }
        {
            var Q0;
            Q0=makeQuery(id+"F31.opPattern","COPY",BODY,{"derivedFrom":makeQuery(id+"F18.opExtrude","SWEPT_BODY",BODY,{"disambiguationData":[OSD([sQuery(id+"F17.wireOp",EDGE,"E18.bottom"),sQuery(id+"F17.wireOp",EDGE,"E18.top"),sQuery(id+"F17.wireOp",EDGE,"E18.left"),sQuery(id+"F17.wireOp",EDGE,"E18.right")])]}),"instanceName":"1"});
            var Q1;
            Q1=makeQuery(id+"F11.opExtrude","SWEPT_BODY",BODY,{"disambiguationData":[OSD([sQuery(id+"F10.wireOp",EDGE,"E12.bottom"),sQuery(id+"F10.wireOp",EDGE,"E12.top"),sQuery(id+"F10.wireOp",EDGE,"E12.left"),sQuery(id+"F10.wireOp",EDGE,"E12.right")])]});
            var Q2;
            Q2=makeQuery(id+"F29.opPattern","COPY",BODY,{"derivedFrom":makeQuery(id+"F11.opExtrude","SWEPT_BODY",BODY,{"disambiguationData":[OSD([sQuery(id+"F10.wireOp",EDGE,"E12.bottom"),sQuery(id+"F10.wireOp",EDGE,"E12.top"),sQuery(id+"F10.wireOp",EDGE,"E12.left"),sQuery(id+"F10.wireOp",EDGE,"E12.right")])]}),"instanceName":"1"});
            booleanBodies(context, id + "F35", {"operationType" : BooleanOperationType.SUBTRACTION, "tools" : qUnion([Q0]), "targets" : qUnion([Q1, Q2]), "keepTools" : true});
        }
        {
            var Q0;
            Q0=makeQuery(id+"F31.opPattern","COPY",FACE,{"derivedFrom":makeQuery(id+"F22.boolean.opBoolean","MERGE",FACE,{"derivedFrom":[makeQuery(id+"F18.opExtrude","CAP_FACE",FACE,{"disambiguationData":[OSD([sQuery(id+"F17.wireOp",EDGE,"E18.bottom"),sQuery(id+"F17.wireOp",EDGE,"E18.top"),sQuery(id+"F17.wireOp",EDGE,"E18.left"),sQuery(id+"F17.wireOp",EDGE,"E18.right")])],"isStart":true}),makeQuery(id+"F22.opExtrude","CAP_FACE",FACE,{"disambiguationData":[OSD([sQuery(id+"F21.wireOp",EDGE,"E28.bottom"),sQuery(id+"F21.wireOp",EDGE,"E28.top"),sQuery(id+"F21.wireOp",EDGE,"E28.left"),sQuery(id+"F21.wireOp",EDGE,"E28.right")])],"isStart":true}),makeQuery(id+"F22.opExtrude","CAP_FACE",FACE,{"disambiguationData":[OSD([sQuery(id+"F21.wireOp",EDGE,"E29.bottom"),sQuery(id+"F21.wireOp",EDGE,"E29.top"),sQuery(id+"F21.wireOp",EDGE,"E29.left"),sQuery(id+"F21.wireOp",EDGE,"E29.right")])],"isStart":true})]}),"instanceName":"1"});
            var sketch = newSketch(context, id + "F36", { "sketchPlane" : qUnion([Q0])});
            skText(sketch, "E67", { "text": "B", "fontName": "OpenSans-Regular.ttf"});
            const initialGuessF36  = {"E67": [-0.0105, -0.03906, 1, 0, 0.02639]};
            skSetInitialGuess(sketch, initialGuessF36);
            skSolve(sketch);
        }
        {
            var Q0;
            Q0=makeQuery(id+"F11.opExtrude","SWEPT_FACE",FACE,{"disambiguationData":[OSD([sQuery(id+"F10.wireOp",EDGE,"E12.top")])]});
            var sketch = newSketch(context, id + "F37", { "sketchPlane" : qUnion([Q0])});
            skLineSegment(sketch, "E68.bottom", {"start": v(-35.67, 24.65) * mm, "end": v(35.67, 24.65) * mm});
            skLineSegment(sketch, "E68.top", {"start": v(-35.67, -21.65) * mm, "end": v(35.67, -21.65) * mm});
            skLineSegment(sketch, "E68.left", {"start": v(-35.67, 24.65) * mm, "end": v(-35.67, -21.65) * mm});
            skLineSegment(sketch, "E68.right", {"start": v(35.67, 24.65) * mm, "end": v(35.67, -21.65) * mm});
            skSolve(sketch);
        }
        {
            var Q0;
            Q0 = qSketchRegion(id + "F37", true);
            extrude(context, id + "F38", {"entities" : qUnion([Q0]), "oppositeDirection" : true, "depth" : 4.67 * mm, "offsetDistance" : 25.4 * mm});
        }
        {
            var Q0;
            Q0=makeQuery(id+"F11.opExtrude","SWEPT_BODY",BODY,{"disambiguationData":[OSD([sQuery(id+"F10.wireOp",EDGE,"E12.bottom"),sQuery(id+"F10.wireOp",EDGE,"E12.top"),sQuery(id+"F10.wireOp",EDGE,"E12.left"),sQuery(id+"F10.wireOp",EDGE,"E12.right")])]});
            var Q1;
            Q1=makeQuery(id+"F29.opPattern","COPY",BODY,{"derivedFrom":makeQuery(id+"F11.opExtrude","SWEPT_BODY",BODY,{"disambiguationData":[OSD([sQuery(id+"F10.wireOp",EDGE,"E12.bottom"),sQuery(id+"F10.wireOp",EDGE,"E12.top"),sQuery(id+"F10.wireOp",EDGE,"E12.left"),sQuery(id+"F10.wireOp",EDGE,"E12.right")])]}),"instanceName":"1"});
            var Q2;
            Q2=makeQuery(id+"F38.opExtrude","SWEPT_BODY",BODY,{"disambiguationData":[OSD([sQuery(id+"F37.wireOp",EDGE,"E68.bottom"),sQuery(id+"F37.wireOp",EDGE,"E68.top"),sQuery(id+"F37.wireOp",EDGE,"E68.left"),sQuery(id+"F37.wireOp",EDGE,"E68.right")])]});
            booleanBodies(context, id + "F39", {"operationType" : BooleanOperationType.SUBTRACTION, "tools" : qUnion([Q0, Q1]), "targets" : qUnion([Q2]), "keepTools" : true});
        }
        {
            var Q0;
            Q0=makeQuery(id+"F38.opExtrude","CAP_FACE",FACE,{"disambiguationData":[OSD([sQuery(id+"F37.wireOp",EDGE,"E68.bottom"),sQuery(id+"F37.wireOp",EDGE,"E68.top"),sQuery(id+"F37.wireOp",EDGE,"E68.left"),sQuery(id+"F37.wireOp",EDGE,"E68.right")])],"isStart":true});
            var sketch = newSketch(context, id + "F40", { "sketchPlane" : qUnion([Q0])});
            skCircle(sketch, "E69", {"center": v(0, 0) * mm, "radius": 9.53 * mm});
            skSolve(sketch);
        }
        {
            var Q0;
            Q0 = qSketchRegion(id + "F40", true);
            extrude(context, id + "F41", {"entities" : qUnion([Q0]), "operationType" : NewBodyOperationType.REMOVE, "endBound" : BoundingType.THROUGH_ALL, "oppositeDirection" : true, "depth" : 25.4 * mm, "offsetDistance" : 25.4 * mm});
        }
    });
